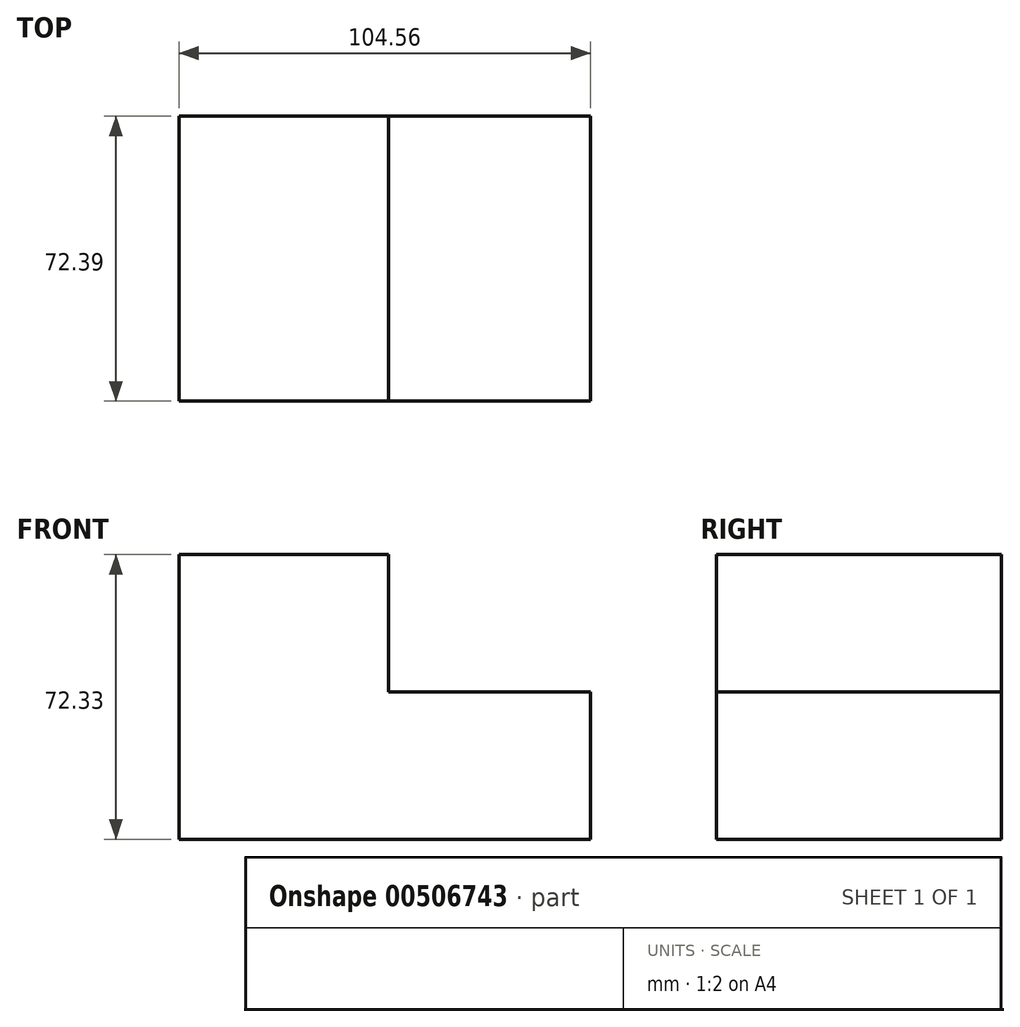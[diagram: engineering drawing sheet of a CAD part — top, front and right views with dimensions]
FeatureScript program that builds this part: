
annotation { "Feature Type Name" : "Feature", "Feature Type Description" : "" }
export const myFeature = defineFeature(function(context is Context, id is Id, definition is map)
    precondition{}
    {
        {
            var Q0;
            Q0=qCreatedBy(makeId("Front.planeOp"),FACE);
            var sketch = newSketch(context, id + "F0", { "sketchPlane" : qUnion([Q0])});
            skLineSegment(sketch, "E0", {"start": v(-5.13, 0) * mm, "end": v(-5.13, 34.93) * mm});
            skLineSegment(sketch, "E1", {"start": v(-5.13, 34.93) * mm, "end": v(-58.38, 34.93) * mm});
            skLineSegment(sketch, "E2", {"start": v(-58.38, 34.93) * mm, "end": v(-58.38, -37.4) * mm});
            skLineSegment(sketch, "E3", {"start": v(-58.38, -37.4) * mm, "end": v(54.82, -37.4) * mm});
            skLineSegment(sketch, "E4", {"start": v(54.82, -37.4) * mm, "end": v(54.82, 0) * mm});
            skLineSegment(sketch, "E5", {"start": v(-5.13, 0) * mm, "end": v(54.82, 0) * mm});
            skSolve(sketch);
        }
        {
            var Q0;
            Q0=makeQuery(id+"F0.imprint","IMPRINT",FACE,{"disambiguationData":[TD([[makeQuery(id+"F0.imprint","IMPRINT",EDGE,{"derivedFrom":sQuery(id+"F0.wireOp",EDGE,"E0")}),1.0]])]});
            extrude(context, id + "F1", {"entities" : qUnion([Q0]), "depth" : 25.4 * mm});
        }
        {
            var Q0;
            Q0=makeQuery(id+"F1.opExtrude","CAP_FACE",FACE,{"disambiguationData":[OSD([sQuery(id+"F0.wireOp",EDGE,"E0"),sQuery(id+"F0.wireOp",EDGE,"E1"),sQuery(id+"F0.wireOp",EDGE,"E2"),sQuery(id+"F0.wireOp",EDGE,"E3"),sQuery(id+"F0.wireOp",EDGE,"E4"),sQuery(id+"F0.wireOp",EDGE,"E5")])],"isStart":false});
            extrude(context, id + "F2", {"entities" : qUnion([Q0]), "operationType" : NewBodyOperationType.ADD, "depth" : 67.82 * mm});
        }
        {
            var Q0;
            Q0=makeQuery(id+"F2.opExtrude","CAP_FACE",FACE,{"disambiguationData":[OSD([sQuery(id+"F0.wireOp",EDGE,"E0"),sQuery(id+"F0.wireOp",EDGE,"E1"),sQuery(id+"F0.wireOp",EDGE,"E2"),sQuery(id+"F0.wireOp",EDGE,"E3"),sQuery(id+"F0.wireOp",EDGE,"E4"),sQuery(id+"F0.wireOp",EDGE,"E5")])],"isStart":false});
            extrude(context, id + "F3", {"entities" : qUnion([Q0]), "operationType" : NewBodyOperationType.REMOVE, "oppositeDirection" : true, "depth" : 20.83 * mm});
        }
        {
            var Q0;
            {var subQ0=sQuery(id+"F0.wireOp",EDGE,"E4");Q0=makeQuery(id+"F2.boolean.opBoolean","MERGE",FACE,{"derivedFrom":[makeQuery(id+"F1.opExtrude","SWEPT_FACE",FACE,{"disambiguationData":[OSD([subQ0])]}),makeQuery(id+"F2.opExtrude","SWEPT_FACE",FACE,{"disambiguationData":[OSD([subQ0])]})]});}
            extrude(context, id + "F4", {"entities" : qUnion([Q0]), "operationType" : NewBodyOperationType.REMOVE, "oppositeDirection" : true, "depth" : 8.64 * mm});
        }
    });
